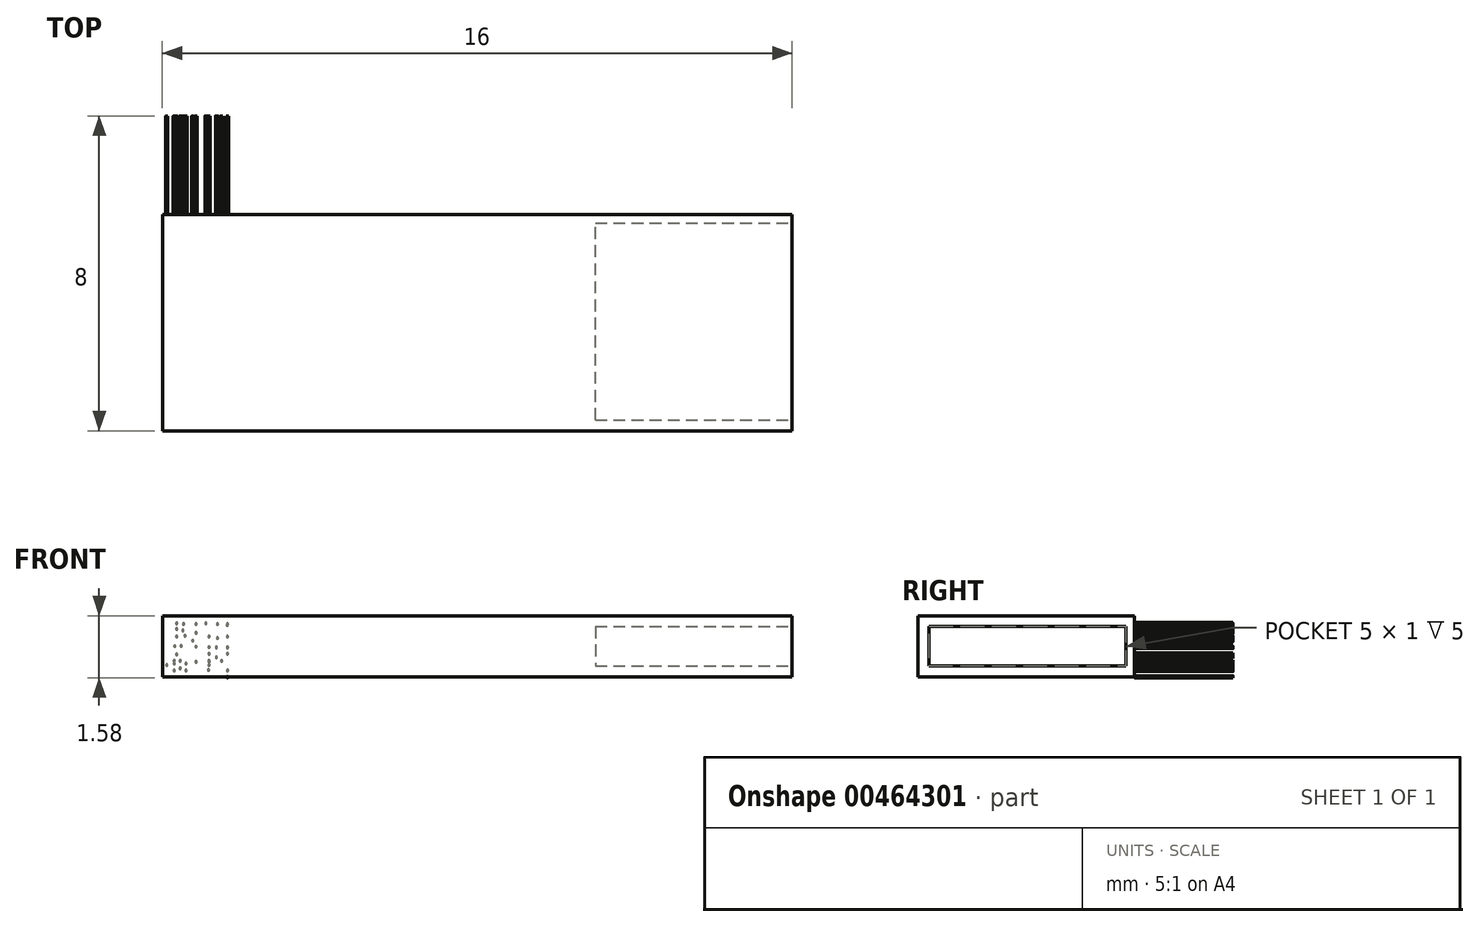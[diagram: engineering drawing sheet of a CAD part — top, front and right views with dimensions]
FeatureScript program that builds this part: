
annotation { "Feature Type Name" : "Feature", "Feature Type Description" : "" }
export const myFeature = defineFeature(function(context is Context, id is Id, definition is map)
    precondition{}
    {
        {
            var Q0;
            Q0=qCreatedBy(makeId("Top.planeOp"),FACE);
            var sketch = newSketch(context, id + "F0", { "sketchPlane" : qUnion([Q0])});
            skLineSegment(sketch, "E0.bottom", {"start": v(-55.4, 33.83) * mm, "end": v(-39.4, 33.83) * mm});
            skLineSegment(sketch, "E0.top", {"start": v(-55.4, 28.33) * mm, "end": v(-39.4, 28.33) * mm});
            skLineSegment(sketch, "E0.left", {"start": v(-55.4, 33.83) * mm, "end": v(-55.4, 28.33) * mm});
            skLineSegment(sketch, "E0.right", {"start": v(-39.4, 33.83) * mm, "end": v(-39.4, 28.33) * mm});
            skSolve(sketch);
        }
        {
            var Q0;
            Q0=makeQuery(id+"F0.imprint","IMPRINT",FACE,{"disambiguationData":[TD([[makeQuery(id+"F0.imprint","IMPRINT",EDGE,{"derivedFrom":sQuery(id+"F0.wireOp",EDGE,"E0.bottom")}),-1.0]])]});
            extrude(context, id + "F1", {"entities" : qUnion([Q0]), "depth" : 1.55 * mm});
        }
        {
            var Q0;
            Q0=makeQuery(id+"F1.opExtrude","SWEPT_FACE",FACE,{"disambiguationData":[OSD([sQuery(id+"F0.wireOp",EDGE,"E0.right")])]});
            var sketch = newSketch(context, id + "F2", { "sketchPlane" : qUnion([Q0])});
            skLineSegment(sketch, "E1.bottom", {"start": v(28.6, 1.28) * mm, "end": v(33.6, 1.28) * mm});
            skLineSegment(sketch, "E1.top", {"start": v(28.6, 0.28) * mm, "end": v(33.6, 0.28) * mm});
            skLineSegment(sketch, "E1.left", {"start": v(28.6, 1.28) * mm, "end": v(28.6, 0.28) * mm});
            skLineSegment(sketch, "E1.right", {"start": v(33.6, 1.28) * mm, "end": v(33.6, 0.28) * mm});
            skSolve(sketch);
        }
        {
            var Q0;
            Q0=makeQuery(id+"F2.imprint","IMPRINT",FACE,{"disambiguationData":[TD([[makeQuery(id+"F2.imprint","IMPRINT",EDGE,{"derivedFrom":sQuery(id+"F2.wireOp",EDGE,"E1.bottom")}),-1.0]])]});
            extrude(context, id + "F3", {"entities" : qUnion([Q0]), "operationType" : NewBodyOperationType.REMOVE, "oppositeDirection" : true, "depth" : 5 * mm});
        }
        {
            var Q0;
            Q0=makeQuery(id+"F1.opExtrude","SWEPT_FACE",FACE,{"disambiguationData":[OSD([sQuery(id+"F0.wireOp",EDGE,"E0.bottom")])]});
            var sketch = newSketch(context, id + "F4", { "sketchPlane" : qUnion([Q0])});
            skSolve(sketch);
        }
        {
            var Q0;
            {var subQ0=sQuery(id+"F0.wireOp",EDGE,"E0.bottom");Q0=makeQuery(id+"F4.imprint","IMPRINT",FACE,{"disambiguationData":[TD([[makeQuery(id+"F4.imprint","IMPRINT",EDGE,{"derivedFrom":makeQuery(id+"F1.opExtrude","CAP_EDGE",EDGE,{"disambiguationData":[OSD([subQ0])],"isStart":true})}),-1.0]])]});}
            var sketch = newSketch(context, id + "F5", { "sketchPlane" : qUnion([Q0])});
            skCircle(sketch, "E2", {"center": v(54.87, 1.34) * mm, "radius": 0.03 * mm});
            skCircle(sketch, "E3", {"center": v(54.89, 1.18) * mm, "radius": 0.03 * mm});
            skCircle(sketch, "E4", {"center": v(55.04, 1.02) * mm, "radius": 0.03 * mm});
            skCircle(sketch, "E5", {"center": v(55.04, 1.21) * mm, "radius": 0.03 * mm});
            skCircle(sketch, "E6", {"center": v(54.83, 1.04) * mm, "radius": 0.02 * mm});
            skCircle(sketch, "E7", {"center": v(54.93, 0.78) * mm, "radius": 0.03 * mm});
            skCircle(sketch, "E8", {"center": v(55.1, 0.78) * mm, "radius": 0.03 * mm});
            skCircle(sketch, "E9", {"center": v(54.22, 0.58) * mm, "radius": 0.03 * mm});
            skCircle(sketch, "E10", {"center": v(54.55, 0.76) * mm, "radius": 0.03 * mm});
            skCircle(sketch, "E11", {"center": v(54.64, 0.92) * mm, "radius": 0.03 * mm});
            skCircle(sketch, "E12", {"center": v(54.55, 1.12) * mm, "radius": 0.03 * mm});
            skCircle(sketch, "E13", {"center": v(55.3, 0.3) * mm, "radius": 0.02 * mm});
            skCircle(sketch, "E14", {"center": v(55.1, 0.33) * mm, "radius": 0.02 * mm});
            skCircle(sketch, "E15", {"center": v(53.75, 0.58) * mm, "radius": 0.02 * mm});
            skCircle(sketch, "E16", {"center": v(53.75, 0.16) * mm, "radius": 0.02 * mm});
            skCircle(sketch, "E17", {"center": v(54.81, 0.16) * mm, "radius": 0.02 * mm});
            skCircle(sketch, "E18", {"center": v(55.1, 0.16) * mm, "radius": 0.02 * mm});
            skCircle(sketch, "E19", {"center": v(55.1, 0.4) * mm, "radius": 0.02 * mm});
            skCircle(sketch, "E20", {"center": v(54.81, 0.34) * mm, "radius": 0.02 * mm});
            skCircle(sketch, "E21", {"center": v(54.95, 0.4) * mm, "radius": 0.03 * mm});
            skCircle(sketch, "E22", {"center": v(54.22, 0.75) * mm, "radius": 0.03 * mm});
            skCircle(sketch, "E23", {"center": v(54.3, 1.36) * mm, "radius": 0.02 * mm});
            skCircle(sketch, "E24", {"center": v(54.95, 0.22) * mm, "radius": 0.03 * mm});
            skCircle(sketch, "E25", {"center": v(54.55, 0.38) * mm, "radius": 0.02 * mm});
            skCircle(sketch, "E26", {"center": v(53.75, 0) * mm, "radius": 0.02 * mm});
            skCircle(sketch, "E27", {"center": v(54.22, 0.3) * mm, "radius": 0.03 * mm});
            skCircle(sketch, "E28", {"center": v(54.55, 1.34) * mm, "radius": 0.03 * mm});
            skCircle(sketch, "E29", {"center": v(53.75, 0.74) * mm, "radius": 0.02 * mm});
            skCircle(sketch, "E30", {"center": v(54.22, 0.4) * mm, "radius": 0.02 * mm});
            skCircle(sketch, "E31", {"center": v(53.75, 0.75) * mm, "radius": 0.02 * mm});
            skCircle(sketch, "E32", {"center": v(53.75, 1.34) * mm, "radius": 0.02 * mm});
            skCircle(sketch, "E33", {"center": v(53.76, 1.31) * mm, "radius": 0.02 * mm});
            skCircle(sketch, "E34", {"center": v(54.04, 0.74) * mm, "radius": 0.02 * mm});
            skCircle(sketch, "E35", {"center": v(53.9, 0.4) * mm, "radius": 0.03 * mm});
            skCircle(sketch, "E36", {"center": v(53.75, 0.16) * mm, "radius": 0.03 * mm});
            skCircle(sketch, "E37", {"center": v(53.75, 0.58) * mm, "radius": 0.03 * mm});
            skCircle(sketch, "E38", {"center": v(54.22, 1.02) * mm, "radius": 0.02 * mm});
            skCircle(sketch, "E39", {"center": v(54, 0.98) * mm, "radius": 0.03 * mm});
            skCircle(sketch, "E40", {"center": v(53.75, 1.02) * mm, "radius": 0.03 * mm});
            skCircle(sketch, "E41", {"center": v(55.04, 1.36) * mm, "radius": 0.02 * mm});
            skCircle(sketch, "E42", {"center": v(55.04, 0.57) * mm, "radius": 0.02 * mm});
            skCircle(sketch, "E43", {"center": v(54.22, 0.38) * mm, "radius": 0.02 * mm});
            skCircle(sketch, "E44", {"center": v(54.24, 0.17) * mm, "radius": 0.03 * mm});
            skCircle(sketch, "E45", {"center": v(54.04, 0.5) * mm, "radius": 0.02 * mm});
            skCircle(sketch, "E46", {"center": v(54, 1.34) * mm, "radius": 0.03 * mm});
            skSolve(sketch);
        }
        {
            var Q0;
            Q0 = qSketchRegion(id + "F5", true);
            extrude(context, id + "F6", {"entities" : qUnion([Q0]), "operationType" : NewBodyOperationType.ADD, "depth" : 2.5 * mm});
        }
    });
